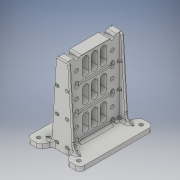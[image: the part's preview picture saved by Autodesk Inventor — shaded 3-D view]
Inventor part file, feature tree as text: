
AUTODESK INVENTOR PART (.ipt)
format: ipt  version: 2018 (Build 220112000, 112)  size: 1,232,896 bytes
history: native  units: in
note: dims shown in document units (in); Inventor stores cm internally (conversion verified against a paired STEP export)
features: extrude x9, sketch x7, fillet x6, mirror x3, hole x2, chamfer x2, pattern_linear x1, emboss x1
ambient origin geometry x8: Origin, YZ Plane, XZ Plane, XY Plane, X Axis, Y Axis, Z Axis, Center Point
bodies: Solid1 (feature_tree)
feature tree (31):
  sketch  "Sketch1"  dims[d0=0.5in d1=3.0in]
  extrude  "Extrusion1"  Depth=3.0in
  sketch  "Sketch2"  dims[d2=4.5in d3=0.25in]
  extrude  "Extrusion2"  Depth=0.25in
  mirror  "Mirror1"
  hole  "Hole1"  [1 undecoded]
  extrude  "Extrusion3"  Depth=2.771in
  pattern_linear  "Rectangular Pattern1"  Count1=3 Spacing1=1.375in
  chamfer  "Chamfer1"  Distance=0.125in
  fillet  "Fillet1"  Radius=0.35in
  extrude  "Extrusion4"  Depth=0.1562in TaperAngle=0.0deg
  extrude  "Extrusion5"  Depth=1.0in
  chamfer  "Chamfer2"  Distance=0.375in
  mirror  "Mirror2"
  fillet  "Fillet2"  Radius=1.1811in
  sketch  "Sketch3"  dims[d4=0.5in d5=3.125in d6=0.0in]
  sketch  "Sketch4"  dims[d7=2.0in d8=2.771in]
  extrude  "Extrusion6"  Depth=2.5in TaperAngle=0.0deg
  extrude  "Extrusion9"  Depth=1.1811in
  hole  "Hole2"  [1 undecoded]
  fillet  "Fillet3"  Radius=0.125in
  extrude  "Extrusion7"  Depth=0.01in
  extrude  "Extrusion8"  Depth=2.0in
  mirror  "Mirror3"
  fillet  "Fillet4"  Radius=0.1in
  fillet  "Fillet6"  Radius=1.1811in
  emboss  "Emboss1"
  fillet  "Fillet5"  Radius=0.01in
  sketch  "Sketch5"  dims[d9=1.2in]
  sketch  "Sketch6"  dims[d11=0.2in d12=1.1811in d14=1.375in d15=0.3937in d17=1.0in]
  sketch  "Sketch7"  dims[d20=0.5in d21=0.125in d22=0.35in d23=0.1562in d24=0.0in d25=0.164in d26=0.328in d27=0.375in d28=0.25in d29=0.5635in d30=0.484in d31=0.8108in d32=1.0in d33=0.375in d34=1.1811in d36=1.375in d37=0.3937in d39=1.0in d41=2.5in d42=0.0in d43=1.1811in d45=0.5in d46=0.0312in d47=0.125in d48=45.0deg d49=0.125in d50=0.375in d52=0.01in d53=2.0in d54=0.1in d55=1.1811in d57=1.375in d58=0.3937in d60=1.0in d62=0.01in d63=0.0625in d64=0.0in d65=0.0625in d66=0.0in d67=0.1875in d68=0.0625in d69=0.125in d70=45.0deg d71=0.125in d72=3.0in d73=4.125in d74=2.25in d75=3.5in d76=3.125in d77=4.25in d78=2.5in d79=3.75in d80=0.0625in d81=0.0in d82=0.201in d83=0.328in d84=0.375in d85=0.25in d86=0.5635in d87=0.484in d88=0.8108in d89=0.25in d90=0.15in d91=0.075in d92=0.5in d93=0.7874in d95=1.375in d96=0.3937in d98=1.0in d100=0.0625in d101=0.0in d102=0.5in d103=0.0625in d104=0.7874in d106=1.375in d107=0.3937in d109=1.0in d111=0.0625in d112=0.0in d113=0.0312in d114=0.125in d115=1.375in d116=60.0deg d117=0.5in d118=0.0625in d119=0.0in d120=0.7874in d122=1.375in d123=0.3937in d125=1.0in d127=0.125in d128=0.0625in d129=0.0157in d130=0.0in]
note: 2 required parameter values undecoded (feature->parameter linkage not recoverable at this tier; creation-order binding heuristic only, values carry confidence <= 0.55)
